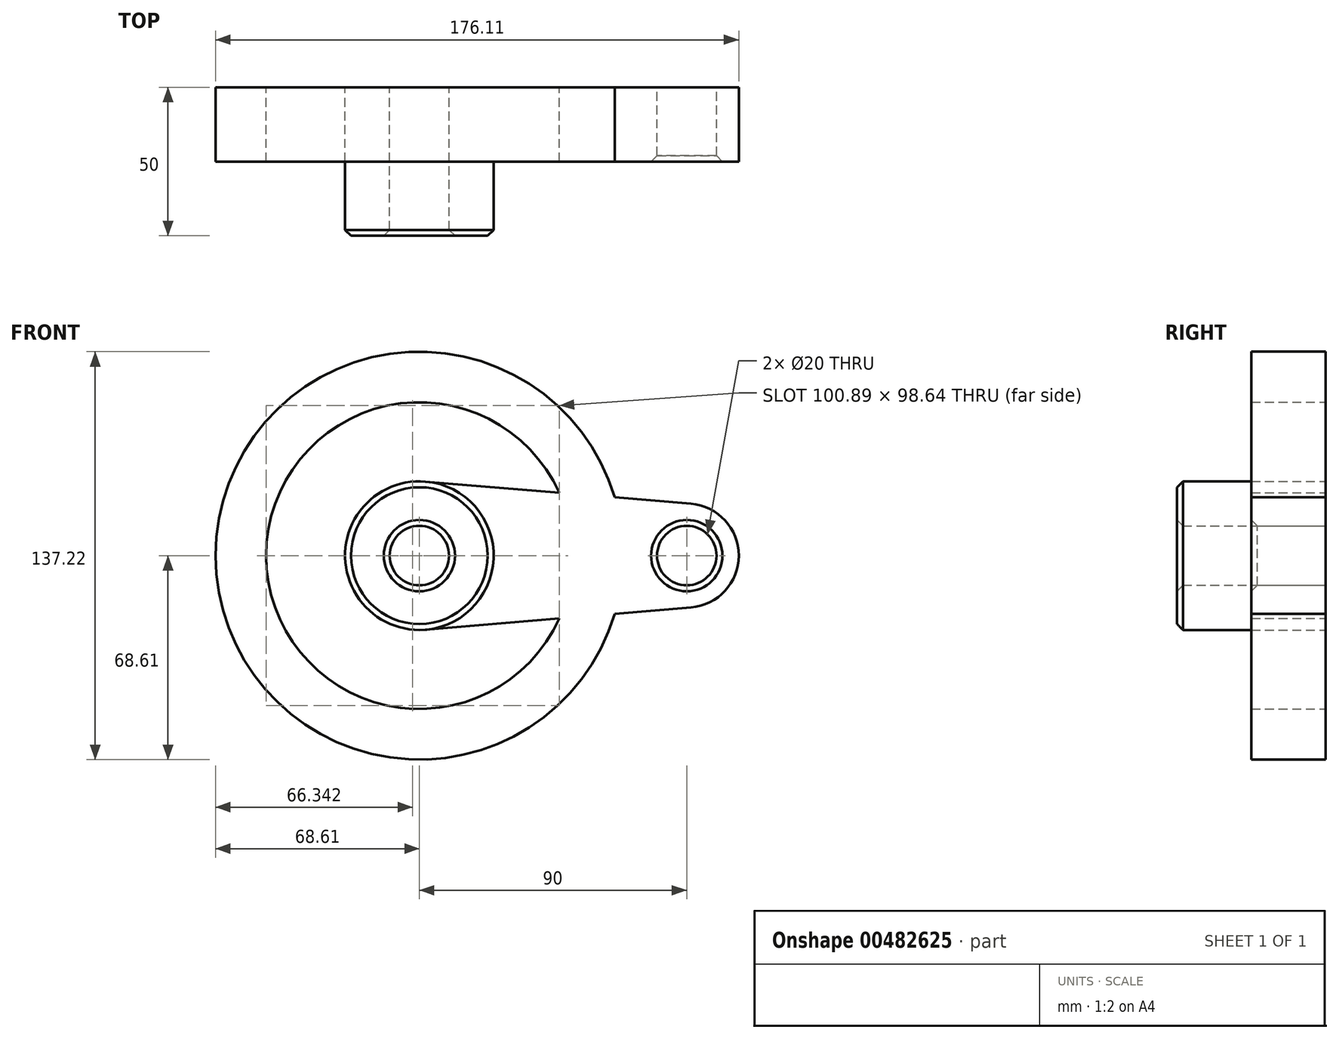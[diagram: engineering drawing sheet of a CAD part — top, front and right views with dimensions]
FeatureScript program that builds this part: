
annotation { "Feature Type Name" : "Feature", "Feature Type Description" : "" }
export const myFeature = defineFeature(function(context is Context, id is Id, definition is map)
    precondition{}
    {
        {
            var Q0;
            Q0=qCreatedBy(makeId("Front.planeOp"),FACE);
            var sketch = newSketch(context, id + "F0", { "sketchPlane" : qUnion([Q0])});
            skCircle(sketch, "E0", {"center": v(0, 0) * mm, "radius": 25 * mm});
            skCircle(sketch, "E1", {"center": v(90, 0) * mm, "radius": 17.5 * mm});
            skLineSegment(sketch, "E2", {"start": v(2.08, 24.91) * mm, "end": v(91.46, 17.44) * mm});
            skLineSegment(sketch, "E3", {"start": v(2.08, -24.91) * mm, "end": v(91.46, -17.44) * mm});
            skCircle(sketch, "E4", {"center": v(0, 0) * mm, "radius": 10 * mm});
            skCircle(sketch, "E5", {"center": v(90, 0) * mm, "radius": 10 * mm});
            skSolve(sketch);
        }
        {
            var Q0;
            Q0=qSketchRegion(id+"F0",true);
            extrude(context, id + "F1", {"entities" : qUnion([Q0]), "depth" : 25 * mm});
        }
        {
            var Q0;
            Q0=makeQuery(id+"F0.imprint","IMPRINT",FACE,{"disambiguationData":[TD([[makeQuery(id+"F0.imprint","IMPRINT",EDGE,{"derivedFrom":sQuery(id+"F0.wireOp",EDGE,"E4")}),-1.0]])]});
            extrude(context, id + "F2", {"entities" : qUnion([Q0]), "operationType" : NewBodyOperationType.ADD, "depth" : 50 * mm});
        }
        {
            var Q0;
            Q0=makeQuery(id+"F2.opExtrude","CAP_EDGE",EDGE,{"disambiguationData":[OSD([sQuery(id+"F0.wireOp",EDGE,"E0")])],"isStart":false});
            var Q1;
            Q1=makeQuery(id+"F2.opExtrude","CAP_EDGE",EDGE,{"disambiguationData":[OSD([sQuery(id+"F0.wireOp",EDGE,"E4")])],"isStart":false});
            var Q2;
            Q2=makeQuery(id+"F1.opExtrude","CAP_EDGE",EDGE,{"disambiguationData":[OSD([sQuery(id+"F0.wireOp",EDGE,"E5")])],"isStart":false});
            chamfer(context, id + "F3", {"entities" : qUnion([Q0, Q1, Q2]), "width" : 2 * mm, "tangentPropagation" : true});
        }
        {
            var Q0;
            Q0=qCreatedBy(makeId("Front.planeOp"),FACE);
            var sketch = newSketch(context, id + "F4", { "sketchPlane" : qUnion([Q0])});
            skCircle(sketch, "E6", {"center": v(0, 0) * mm, "radius": 51.59 * mm});
            skCircle(sketch, "E7", {"center": v(0, 0) * mm, "radius": 68.61 * mm});
            skSolve(sketch);
        }
        {
            var Q0;
            Q0=makeQuery(id+"F4.imprint","IMPRINT",FACE,{"disambiguationData":[TD([[makeQuery(id+"F4.imprint","IMPRINT",EDGE,{"derivedFrom":sQuery(id+"F4.wireOp",EDGE,"E6")}),-1.0]])]});
            extrude(context, id + "F5", {"entities" : qUnion([Q0]), "operationType" : NewBodyOperationType.ADD, "depth" : 25 * mm});
        }
    });
